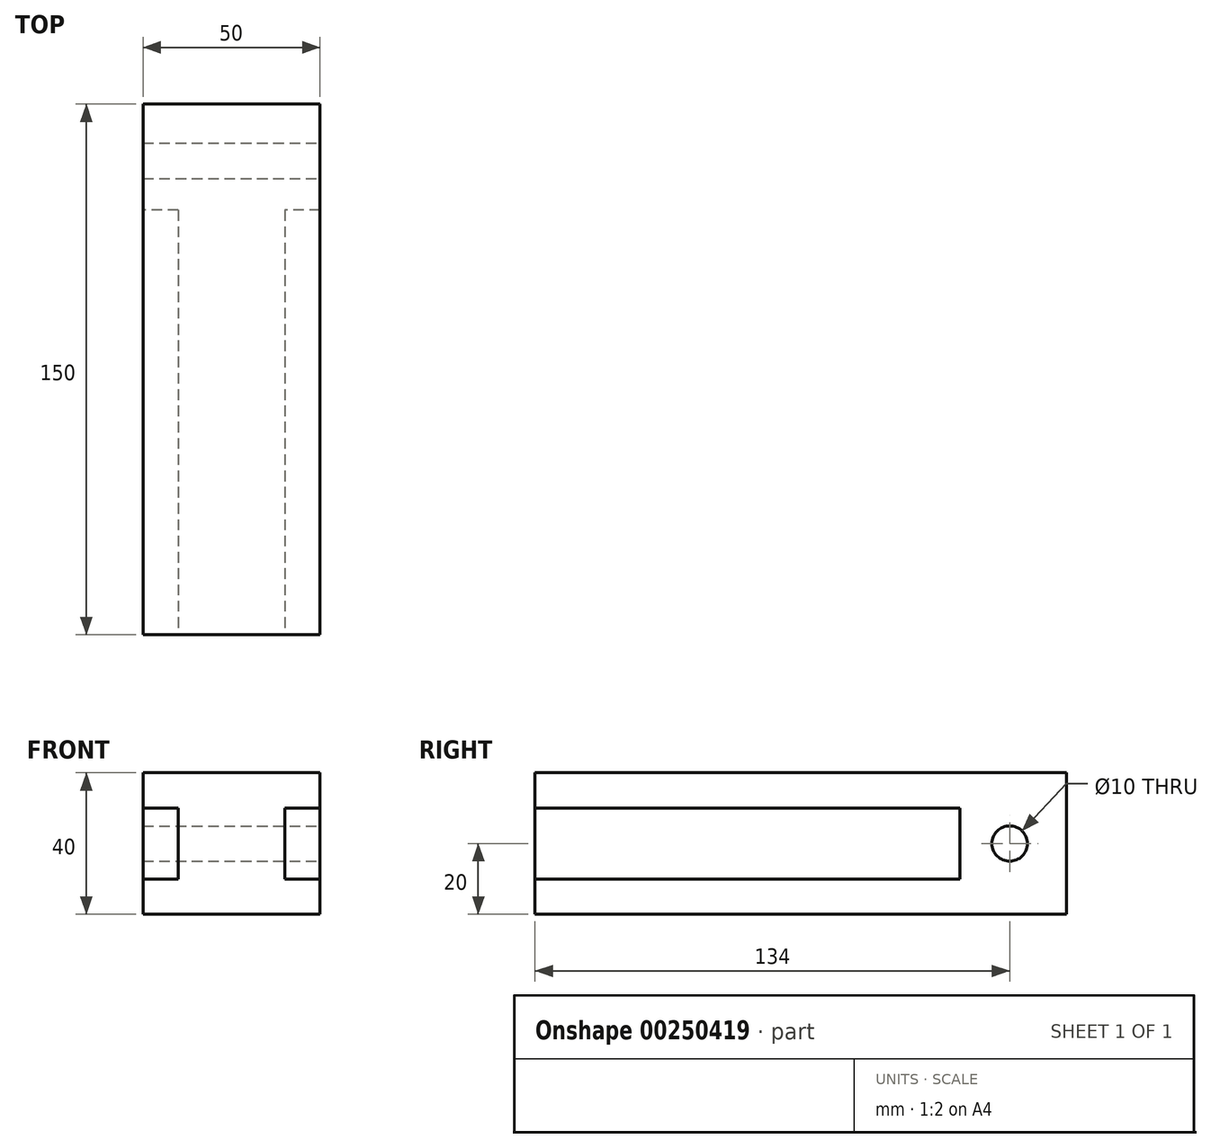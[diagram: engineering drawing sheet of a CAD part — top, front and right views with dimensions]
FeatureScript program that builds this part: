
annotation { "Feature Type Name" : "Feature", "Feature Type Description" : "" }
export const myFeature = defineFeature(function(context is Context, id is Id, definition is map)
    precondition{}
    {
        {
            var Q0;
            Q0=qCreatedBy(makeId("Front.planeOp"),FACE);
            var sketch = newSketch(context, id + "F0", { "sketchPlane" : qUnion([Q0])});
            skLineSegment(sketch, "E0.bottom", {"start": v(25, 20) * mm, "end": v(-25, 20) * mm});
            skLineSegment(sketch, "E0.top", {"start": v(25, -20) * mm, "end": v(-25, -20) * mm});
            skLineSegment(sketch, "E0.left", {"start": v(25, 20) * mm, "end": v(25, -20) * mm});
            skLineSegment(sketch, "E0.right", {"start": v(-25, 20) * mm, "end": v(-25, -20) * mm});
            skPoint(sketch, "E0.middle", {"position": v(0, 0) * mm});
            skSolve(sketch);
        }
        {
            var Q0;
            Q0 = qSketchRegion(id + "F0", true);
            extrude(context, id + "F1", {"entities" : qUnion([Q0]), "depth" : 150 * mm});
        }
        {
            var Q0;
            Q0=makeQuery(id+"F1.opExtrude","SWEPT_FACE",FACE,{"disambiguationData":[OSD([sQuery(id+"F0.wireOp",EDGE,"E0.left")])]});
            var sketch = newSketch(context, id + "F2", { "sketchPlane" : qUnion([Q0])});
            skCircle(sketch, "E1", {"center": v(-16, 0) * mm, "radius": 5 * mm});
            skSolve(sketch);
        }
        {
            var Q0;
            Q0 = qSketchRegion(id + "F2", true);
            extrude(context, id + "F3", {"entities" : qUnion([Q0]), "oppositeDirection" : true, "depth" : 104 * mm});
        }
        {
            var Q0;
            Q0=makeQuery(id+"F3.opExtrude","SWEPT_BODY",BODY,{"disambiguationData":[OSD([sQuery(id+"F2.wireOp",EDGE,"E1")])]});
            var Q1;
            Q1=makeQuery(id+"F1.opExtrude","SWEPT_BODY",BODY,{"disambiguationData":[OSD([sQuery(id+"F0.wireOp",EDGE,"E0.bottom"),sQuery(id+"F0.wireOp",EDGE,"E0.top"),sQuery(id+"F0.wireOp",EDGE,"E0.left"),sQuery(id+"F0.wireOp",EDGE,"E0.right")])]});
            booleanBodies(context, id + "F4", {"operationType" : BooleanOperationType.SUBTRACTION, "tools" : qUnion([Q0]), "targets" : qUnion([Q1])});
        }
        {
            var Q0;
            Q0=makeQuery(id+"F1.opExtrude","CAP_FACE",FACE,{"disambiguationData":[OSD([sQuery(id+"F0.wireOp",EDGE,"E0.bottom"),sQuery(id+"F0.wireOp",EDGE,"E0.top"),sQuery(id+"F0.wireOp",EDGE,"E0.left"),sQuery(id+"F0.wireOp",EDGE,"E0.right")])],"isStart":false});
            var sketch = newSketch(context, id + "F5", { "sketchPlane" : qUnion([Q0])});
            skLineSegment(sketch, "E2.top", {"start": v(-30, -10) * mm, "end": v(-15, -10) * mm});
            skLineSegment(sketch, "E2.right", {"start": v(-15, 10) * mm, "end": v(-15, -10) * mm});
            skLineSegment(sketch, "E3", {"start": v(0, -23.94) * mm, "end": v(0, 29.14) * mm, "construction": true});
            skLineSegment(sketch, "E4.MirrorCS", {"start": v(15, 10) * mm, "end": v(15, -10) * mm});
            skLineSegment(sketch, "E5.MirrorCS", {"start": v(30, -10) * mm, "end": v(15, -10) * mm});
            skLineSegment(sketch, "E6", {"start": v(30, -10) * mm, "end": v(30, 10) * mm});
            skLineSegment(sketch, "E7", {"start": v(30, 10) * mm, "end": v(15, 10) * mm});
            skLineSegment(sketch, "E8", {"start": v(-30, 10) * mm, "end": v(-30, -10) * mm});
            skLineSegment(sketch, "E9.trimOffspring", {"start": v(-15, 10) * mm, "end": v(-30, 10) * mm});
            skSolve(sketch);
        }
        {
            var Q0;
            Q0 = qSketchRegion(id + "F5", true);
            extrude(context, id + "F6", {"entities" : qUnion([Q0]), "oppositeDirection" : true, "depth" : 120 * mm});
        }
        {
            var Q0;
            Q0=makeQuery(id+"F6.opExtrude","SWEPT_BODY",BODY,{"disambiguationData":[OSD([sQuery(id+"F5.wireOp",EDGE,"E4.MirrorCS"),sQuery(id+"F5.wireOp",EDGE,"E5.MirrorCS"),sQuery(id+"F5.wireOp",EDGE,"E6"),sQuery(id+"F5.wireOp",EDGE,"E7")])]});
            var Q1;
            Q1=makeQuery(id+"F6.opExtrude","SWEPT_BODY",BODY,{"disambiguationData":[OSD([sQuery(id+"F5.wireOp",EDGE,"E2.top"),sQuery(id+"F5.wireOp",EDGE,"E2.right"),sQuery(id+"F5.wireOp",EDGE,"E8"),sQuery(id+"F5.wireOp",EDGE,"E9.trimOffspring")])]});
            var Q2;
            Q2=makeQuery(id+"F1.opExtrude","SWEPT_BODY",BODY,{"disambiguationData":[OSD([sQuery(id+"F0.wireOp",EDGE,"E0.bottom"),sQuery(id+"F0.wireOp",EDGE,"E0.top"),sQuery(id+"F0.wireOp",EDGE,"E0.left"),sQuery(id+"F0.wireOp",EDGE,"E0.right")])]});
            booleanBodies(context, id + "F7", {"operationType" : BooleanOperationType.SUBTRACTION, "tools" : qUnion([Q0, Q1]), "targets" : qUnion([Q2])});
        }
    });
